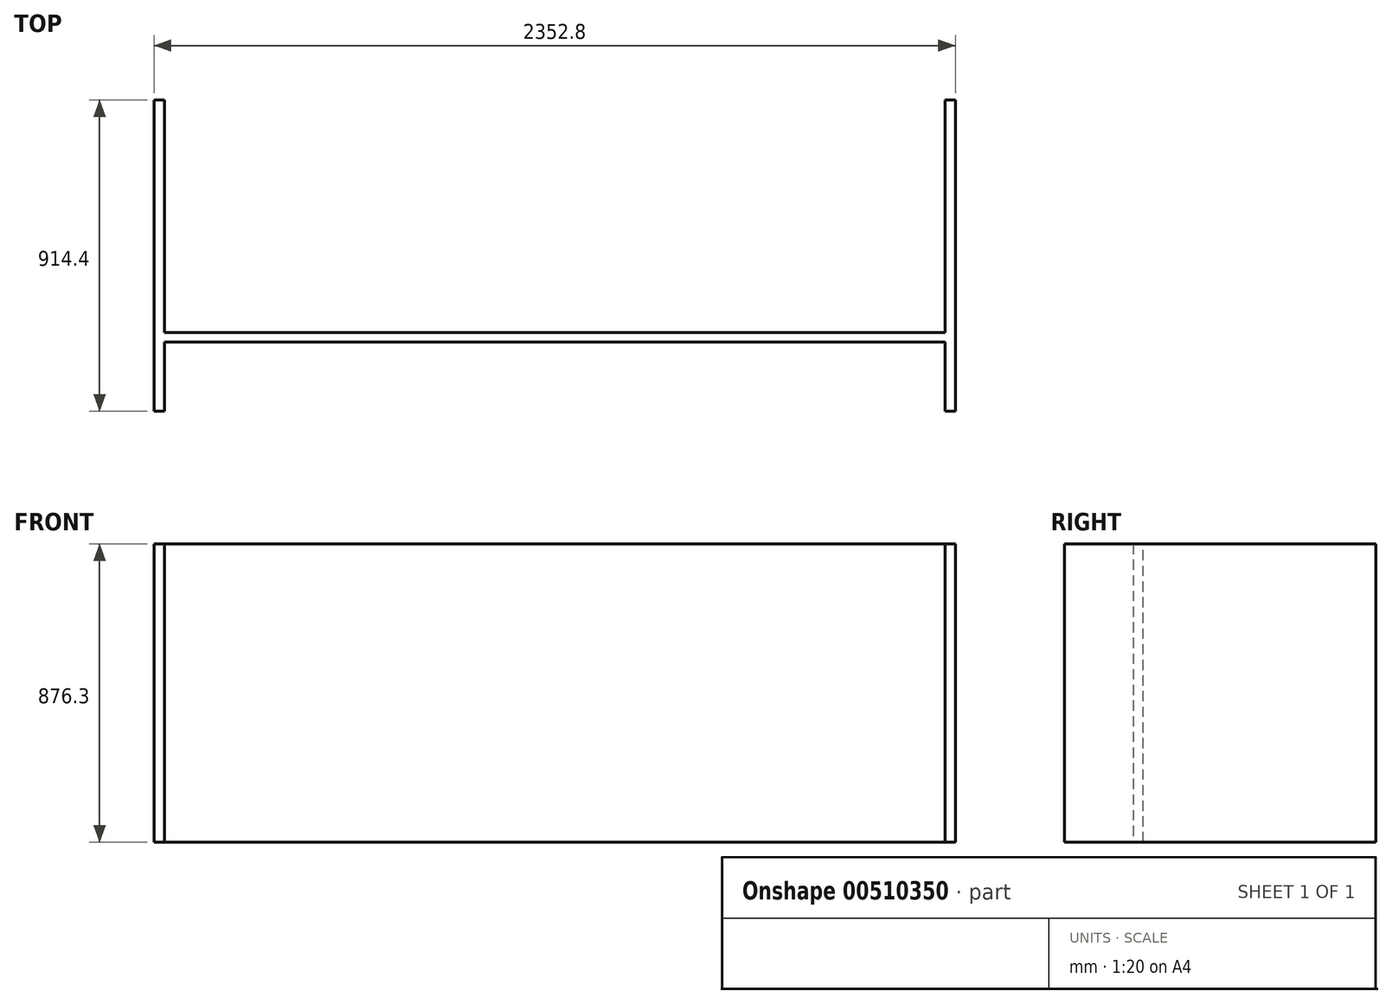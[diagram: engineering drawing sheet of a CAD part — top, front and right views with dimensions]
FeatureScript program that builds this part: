
annotation { "Feature Type Name" : "Feature", "Feature Type Description" : "" }
export const myFeature = defineFeature(function(context is Context, id is Id, definition is map)
    precondition{}
    {
        {
            var Q0;
            Q0=qCreatedBy(makeId("Right.planeOp"),FACE);
            var sketch = newSketch(context, id + "F0", { "sketchPlane" : qUnion([Q0])});
            skLineSegment(sketch, "E0.bottom", {"start": v(457.2, 438.15) * mm, "end": v(-457.2, 438.15) * mm});
            skLineSegment(sketch, "E0.top", {"start": v(457.2, -438.15) * mm, "end": v(-457.2, -438.15) * mm});
            skLineSegment(sketch, "E0.left", {"start": v(457.2, 438.15) * mm, "end": v(457.2, -438.15) * mm});
            skLineSegment(sketch, "E0.right", {"start": v(-457.2, 438.15) * mm, "end": v(-457.2, -438.15) * mm});
            skPoint(sketch, "E0.middle", {"position": v(0, 0) * mm});
            skSolve(sketch);
        }
        {
            var Q0;
            Q0 = qSketchRegion(id + "F0", true);
            extrude(context, id + "F1", {"entities" : qUnion([Q0]), "depth" : 30.23 * mm});
        }
        {
            var Q0;
            Q0=makeQuery(id+"F1.opExtrude","CAP_FACE",FACE,{"disambiguationData":[OSD([sQuery(id+"F0.wireOp",EDGE,"E0.bottom"),sQuery(id+"F0.wireOp",EDGE,"E0.top"),sQuery(id+"F0.wireOp",EDGE,"E0.left"),sQuery(id+"F0.wireOp",EDGE,"E0.right")])],"isStart":false});
            var sketch = newSketch(context, id + "F2", { "sketchPlane" : qUnion([Q0])});
            skLineSegment(sketch, "E1", {"start": v(-457.2, 438.15) * mm, "end": v(-254, 438.15) * mm});
            skLineSegment(sketch, "E2", {"start": v(-254, 438.15) * mm, "end": v(-254, -438.15) * mm});
            skLineSegment(sketch, "E3", {"start": v(-254, -438.15) * mm, "end": v(-225.42, -438.15) * mm});
            skLineSegment(sketch, "E4", {"start": v(-225.42, -438.15) * mm, "end": v(-225.42, 438.15) * mm});
            skLineSegment(sketch, "E5", {"start": v(-225.42, 438.15) * mm, "end": v(-254, 438.15) * mm});
            skSolve(sketch);
        }
        {
            var Q0;
            Q0 = qSketchRegion(id + "F2", true);
            extrude(context, id + "F3", {"entities" : qUnion([Q0]), "operationType" : NewBodyOperationType.ADD, "depth" : 2292.35 * mm});
        }
        {
            var Q0;
            Q0=makeQuery(id+"F3.boolean.opBoolean","MERGE",FACE,{"derivedFrom":[makeQuery(id+"F1.opExtrude","SWEPT_FACE",FACE,{"disambiguationData":[OSD([sQuery(id+"F0.wireOp",EDGE,"E0.bottom")])]}),makeQuery(id+"F3.opExtrude","SWEPT_FACE",FACE,{"disambiguationData":[OSD([sQuery(id+"F2.wireOp",EDGE,"E5")])]})]});
            var sketch = newSketch(context, id + "F4", { "sketchPlane" : qUnion([Q0])});
            skLineSegment(sketch, "E6", {"start": v(2322.58, -254) * mm, "end": v(2322.58, -457.2) * mm});
            skLineSegment(sketch, "E7", {"start": v(2322.58, -457.2) * mm, "end": v(2352.8, -457.2) * mm});
            skLineSegment(sketch, "E8", {"start": v(2352.8, -457.2) * mm, "end": v(2352.8, 457.2) * mm});
            skLineSegment(sketch, "E9", {"start": v(2352.8, 457.2) * mm, "end": v(2322.58, 457.2) * mm});
            skLineSegment(sketch, "E10", {"start": v(2322.58, 457.2) * mm, "end": v(2322.58, -225.42) * mm});
            skSolve(sketch);
        }
        {
            var Q0;
            Q0=makeQuery(id+"F4.imprint","IMPRINT",FACE,{"disambiguationData":[TD([[makeQuery(id+"F4.imprint","IMPRINT",EDGE,{"derivedFrom":sQuery(id+"F4.wireOp",EDGE,"E6")}),1.0]])]});
            extrude(context, id + "F5", {"entities" : qUnion([Q0]), "operationType" : NewBodyOperationType.ADD, "oppositeDirection" : true, "depth" : 876.3 * mm});
        }
    });
